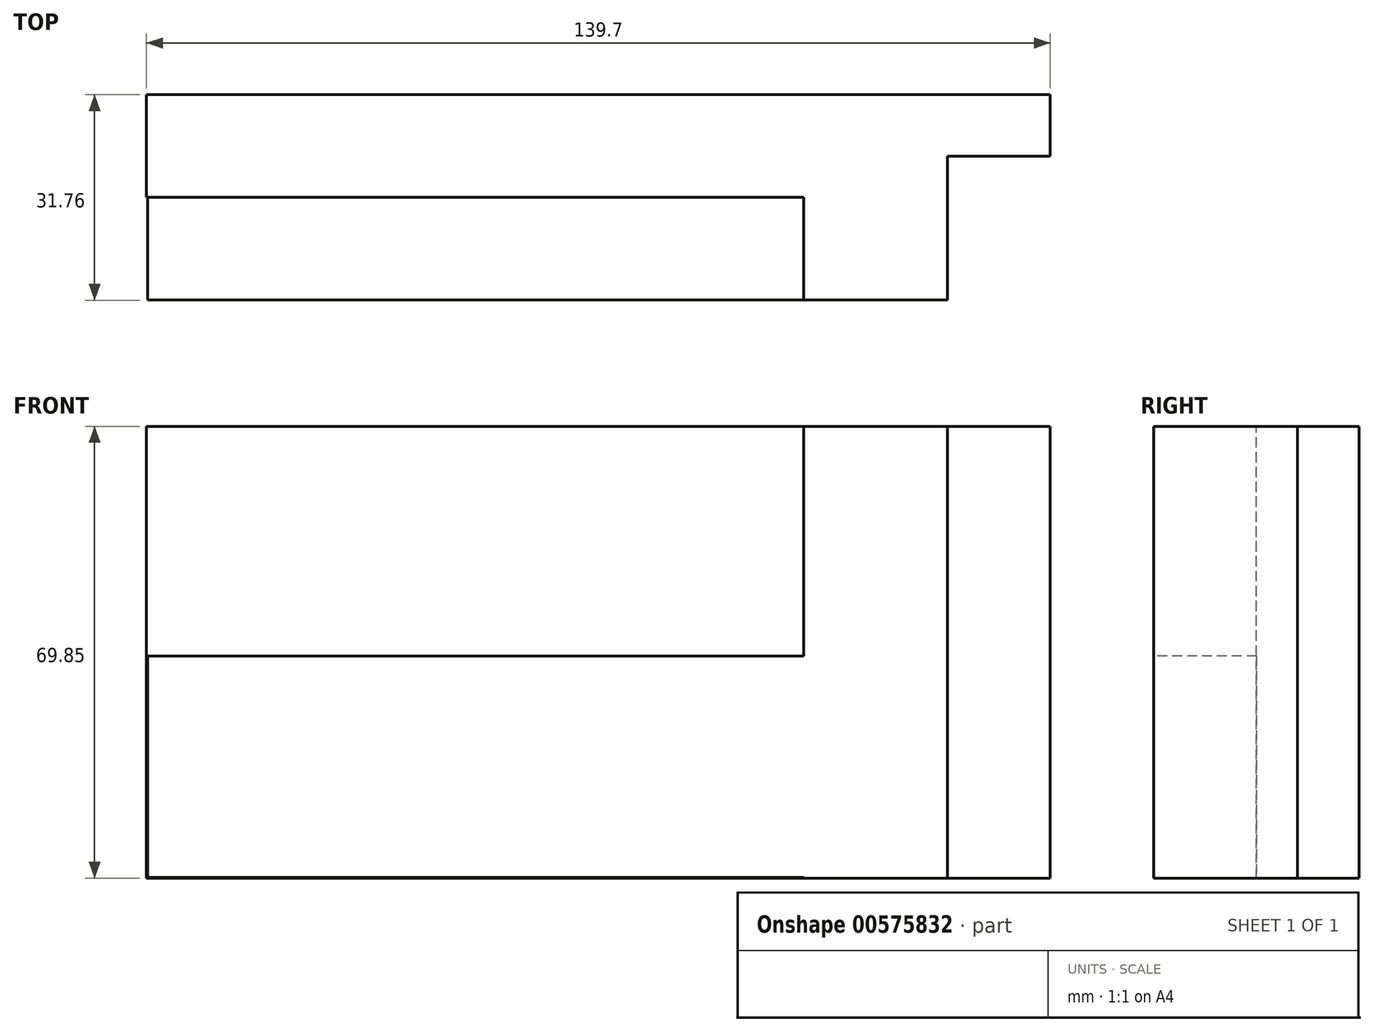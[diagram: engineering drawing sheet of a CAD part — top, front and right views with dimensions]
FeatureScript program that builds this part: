
annotation { "Feature Type Name" : "Feature", "Feature Type Description" : "" }
export const myFeature = defineFeature(function(context is Context, id is Id, definition is map)
    precondition{}
    {
        {
            var Q0;
            Q0=qCreatedBy(makeId("Top.planeOp"),FACE);
            var sketch = newSketch(context, id + "F0", { "sketchPlane" : qUnion([Q0])});
            skLineSegment(sketch, "E0", {"start": v(-72.08, 15.88) * mm, "end": v(-72.08, 0) * mm});
            skLineSegment(sketch, "E1", {"start": v(-72.08, 15.88) * mm, "end": v(67.62, 15.88) * mm});
            skLineSegment(sketch, "E2", {"start": v(67.62, 15.88) * mm, "end": v(67.62, 6.35) * mm});
            skLineSegment(sketch, "E3", {"start": v(67.62, 6.35) * mm, "end": v(51.74, 6.35) * mm});
            skLineSegment(sketch, "E4", {"start": v(-72.08, 0) * mm, "end": v(23.17, 0) * mm});
            skLineSegment(sketch, "E5", {"start": v(51.74, 6.35) * mm, "end": v(29.52, 6.35) * mm});
            skLineSegment(sketch, "E6", {"start": v(23.17, 0) * mm, "end": v(29.52, 0) * mm});
            skLineSegment(sketch, "E7", {"start": v(29.52, 0) * mm, "end": v(29.52, 6.35) * mm});
            skSolve(sketch);
        }
        {
            var Q0;
            Q0 = qSketchRegion(id + "F0", true);
            extrude(context, id + "F1", {"entities" : qUnion([Q0]), "oppositeDirection" : true, "depth" : 69.85 * mm, "offsetDistance" : 25.4 * mm});
        }
        {
            var Q0;
            Q0=qCreatedBy(makeId("Front.planeOp"),FACE);
            var sketch = newSketch(context, id + "F2", { "sketchPlane" : qUnion([Q0])});
            skLineSegment(sketch, "E8", {"start": v(-71.87, -35.5) * mm, "end": v(-71.87, -69.76) * mm});
            skPoint(sketch, "E9.start.orphan", {"position": v(28.8, 0) * mm});
            skLineSegment(sketch, "E10", {"start": v(-71.87, -35.5) * mm, "end": v(29.73, -35.5) * mm});
            skLineSegment(sketch, "E11", {"start": v(29.73, 0) * mm, "end": v(28.8, 0) * mm});
            skPoint(sketch, "E12.end.orphan", {"position": v(29.73, 0) * mm});
            skPoint(sketch, "E13.end.orphan", {"position": v(51, 0) * mm});
            skLineSegment(sketch, "E14", {"start": v(-71.87, -69.76) * mm, "end": v(29.73, -69.76) * mm});
            skLineSegment(sketch, "E15", {"start": v(29.73, -69.76) * mm, "end": v(29.73, -35.5) * mm});
            skSolve(sketch);
        }
        {
            var Q0;
            Q0 = qSketchRegion(id + "F2", true);
            extrude(context, id + "F3", {"entities" : qUnion([Q0]), "operationType" : NewBodyOperationType.ADD, "depth" : 15.88 * mm, "offsetDistance" : 25.4 * mm});
        }
        {
            var Q0;
            Q0=makeQuery(id+"F1.opExtrude","SWEPT_FACE",FACE,{"disambiguationData":[OSD([sQuery(id+"F0.wireOp",EDGE,"E3"),sQuery(id+"F0.wireOp",EDGE,"E5")])]});
            var sketch = newSketch(context, id + "F4", { "sketchPlane" : qUnion([Q0])});
            skLineSegment(sketch, "E16", {"start": v(29.52, -69.85) * mm, "end": v(51.74, -69.85) * mm});
            skLineSegment(sketch, "E17", {"start": v(29.52, -69.85) * mm, "end": v(29.52, 0) * mm});
            skPoint(sketch, "E18.end.orphan", {"position": v(48.57, 0) * mm});
            skLineSegment(sketch, "E19", {"start": v(51.74, -69.85) * mm, "end": v(51.74, 0) * mm});
            skLineSegment(sketch, "E20", {"start": v(51.74, 0) * mm, "end": v(29.52, 0) * mm});
            skSolve(sketch);
        }
        {
            var Q0;
            Q0 = qSketchRegion(id + "F4", true);
            extrude(context, id + "F5", {"entities" : qUnion([Q0]), "operationType" : NewBodyOperationType.ADD, "depth" : 22.22 * mm, "offsetDistance" : 25.4 * mm});
        }
    });
